# Revit family: Shower-Valve_Trim-KOHLER-MODULO-K-99975T
name_source: partatom
category: Specialty Equipment
revit_build: Autodesk Revit 2017 (Build: 20160225_1515(x64)
units: mm (PartAtom-declared; Revit-internal decimal feet)

## family parameters
Cut with Voids When Loaded = No
Host = Face
OmniClass Number = 23.31.25.00
Part Type = Normal
Room Calculation Point = No
Round Connector Dimension = Use Diameter
Shared = No

## types (2) — shared parameters
ADA Compliant = No
Assembly Code = C1030200
Date Modified = 09/18/2020
Default Elevation = 42"
Description = Smart valve core series Smart formula thermostatic in-wall shower valve core and panel (bins handle)
Finish = Kohler-Metal-CP-Polished_Chrome
Height = 7 1/16"
Length = 4 1/8"
Manufacturer = KOHLER Co.
Master Format 2014 = 10 28 00
Master Format 2014 Name = Toilet, Bath, and Laundry Accessories
Material = Premium Metal Construction
Product Documentation Link = https://files.kohler.com.cn
Product Name = MODULO
Product Page URL = https://www.kohler.com.cn
URL = http://www.kohler.com.cn
WaterSense Certified = No
Width = 5 1/2"

## per-type parameters (varying)
| type | Cross Handle | Lever Handle | Model | Type |
| Cross Handle, CP-Polished Chrome | Yes | No | K-99975T-3A-CP | 1 |
| Lever Handel, CP-Polished Chrome | No | Yes | K-99975T-4A-CP | 2 |

## geometry (parser evidence)
native form markers: Sweep x4
no freeform markers — native parametric forms only
